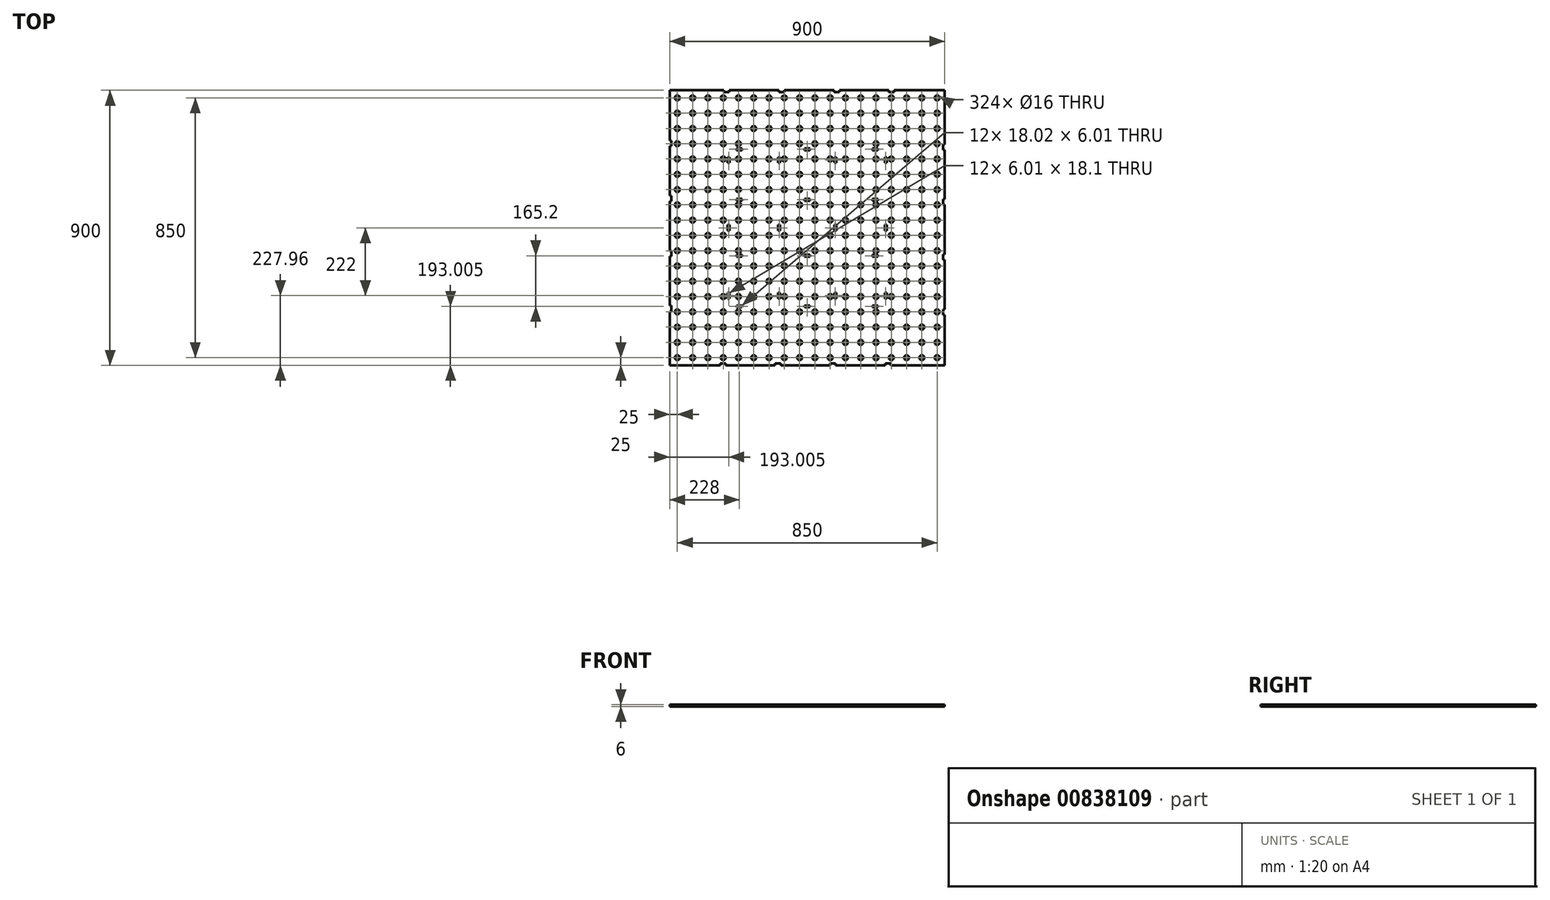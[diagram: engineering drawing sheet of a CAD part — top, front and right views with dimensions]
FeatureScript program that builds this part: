
annotation { "Feature Type Name" : "Feature", "Feature Type Description" : "" }
export const myFeature = defineFeature(function(context is Context, id is Id, definition is map)
    precondition{}
    {
        {
            var Q0;
            Q0=qCreatedBy(makeId("Top.planeOp"),FACE);
            var sketch = newSketch(context, id + "F0", { "sketchPlane" : qUnion([Q0])});
            skCircle(sketch, "E0", {"center": v(0, 0) * mm, "radius": 8 * mm});
            skCircle(sketch, "E1", {"center": v(50, 0) * mm, "radius": 8 * mm});
            skCircle(sketch, "E2", {"center": v(100, 0) * mm, "radius": 8 * mm});
            skCircle(sketch, "E3", {"center": v(0, -50) * mm, "radius": 8 * mm});
            skLineSegment(sketch, "E4", {"start": v(-25, 0.08) * mm, "end": v(875, 0.08) * mm, "construction": true});
            skCircle(sketch, "E5", {"center": v(150, 0.08) * mm, "radius": 8 * mm});
            skCircle(sketch, "E6", {"center": v(200, 0.08) * mm, "radius": 8 * mm});
            skCircle(sketch, "E7", {"center": v(250, 0.08) * mm, "radius": 8 * mm});
            skLineSegment(sketch, "E8", {"start": v(0, 8) * mm, "end": v(0, -874.92) * mm, "construction": true});
            skCircle(sketch, "E9", {"center": v(50, -50) * mm, "radius": 8 * mm});
            skCircle(sketch, "E10", {"center": v(100, -50) * mm, "radius": 8 * mm});
            skCircle(sketch, "E11", {"center": v(150, -50) * mm, "radius": 8 * mm});
            skCircle(sketch, "E12", {"center": v(200, -50) * mm, "radius": 8 * mm});
            skCircle(sketch, "E13", {"center": v(250, -50) * mm, "radius": 8 * mm});
            skCircle(sketch, "E14", {"center": v(0, -100) * mm, "radius": 8 * mm});
            skCircle(sketch, "E15", {"center": v(0, -150) * mm, "radius": 8 * mm});
            skCircle(sketch, "E16", {"center": v(0, -199.92) * mm, "radius": 8 * mm});
            skCircle(sketch, "E17", {"center": v(50, -100) * mm, "radius": 8 * mm});
            skCircle(sketch, "E18", {"center": v(100, -100) * mm, "radius": 8 * mm});
            skCircle(sketch, "E19", {"center": v(50, -150) * mm, "radius": 8 * mm});
            skCircle(sketch, "E20", {"center": v(100, -150) * mm, "radius": 8 * mm});
            skCircle(sketch, "E21", {"center": v(50, -199.92) * mm, "radius": 8 * mm});
            skCircle(sketch, "E22", {"center": v(100, -199.92) * mm, "radius": 8 * mm});
            skCircle(sketch, "E23", {"center": v(150, -100) * mm, "radius": 8 * mm});
            skCircle(sketch, "E24", {"center": v(150, -150) * mm, "radius": 8 * mm});
            skPoint(sketch, "E25.center.orphan", {"position": v(150, -199.92) * mm});
            skCircle(sketch, "E26", {"center": v(150, -199.92) * mm, "radius": 8 * mm});
            skCircle(sketch, "E27", {"center": v(200, -100) * mm, "radius": 8 * mm});
            skCircle(sketch, "E28", {"center": v(200, -150) * mm, "radius": 8 * mm});
            skCircle(sketch, "E29", {"center": v(250, -100) * mm, "radius": 8 * mm});
            skCircle(sketch, "E30", {"center": v(250, -150) * mm, "radius": 8 * mm});
            skCircle(sketch, "E31", {"center": v(200, -199.92) * mm, "radius": 8 * mm});
            skCircle(sketch, "E32", {"center": v(250, -199.92) * mm, "radius": 8 * mm});
            skCircle(sketch, "E33", {"center": v(300, 0.08) * mm, "radius": 8 * mm});
            skCircle(sketch, "E34", {"center": v(350, 0.08) * mm, "radius": 8 * mm});
            skCircle(sketch, "E35", {"center": v(400, 0.08) * mm, "radius": 8 * mm});
            skCircle(sketch, "E36", {"center": v(300, -50) * mm, "radius": 8 * mm});
            skCircle(sketch, "E37", {"center": v(350, -50) * mm, "radius": 8 * mm});
            skCircle(sketch, "E38", {"center": v(400, -50) * mm, "radius": 8 * mm});
            skCircle(sketch, "E39", {"center": v(300, -100) * mm, "radius": 8 * mm});
            skCircle(sketch, "E40", {"center": v(350, -100) * mm, "radius": 8 * mm});
            skCircle(sketch, "E41", {"center": v(400, -100) * mm, "radius": 8 * mm});
            skCircle(sketch, "E42", {"center": v(300, -150) * mm, "radius": 8 * mm});
            skCircle(sketch, "E43", {"center": v(350, -150) * mm, "radius": 8 * mm});
            skCircle(sketch, "E44", {"center": v(400, -150) * mm, "radius": 8 * mm});
            skCircle(sketch, "E45", {"center": v(300, -199.92) * mm, "radius": 8 * mm});
            skCircle(sketch, "E46", {"center": v(350, -199.92) * mm, "radius": 8 * mm});
            skCircle(sketch, "E47", {"center": v(400, -199.92) * mm, "radius": 8 * mm});
            skCircle(sketch, "E48", {"center": v(0, -249.92) * mm, "radius": 8 * mm});
            skCircle(sketch, "E49", {"center": v(0, -299.92) * mm, "radius": 8 * mm});
            skCircle(sketch, "E50", {"center": v(0, -349.92) * mm, "radius": 8 * mm});
            skCircle(sketch, "E51", {"center": v(50, -249.92) * mm, "radius": 8 * mm});
            skCircle(sketch, "E52", {"center": v(100, -249.92) * mm, "radius": 8 * mm});
            skCircle(sketch, "E53", {"center": v(50, -299.92) * mm, "radius": 8 * mm});
            skCircle(sketch, "E54", {"center": v(100, -299.92) * mm, "radius": 8 * mm});
            skCircle(sketch, "E55", {"center": v(50, -349.92) * mm, "radius": 8 * mm});
            skCircle(sketch, "E56", {"center": v(100, -349.92) * mm, "radius": 8 * mm});
            skCircle(sketch, "E57", {"center": v(200, -249.92) * mm, "radius": 8 * mm});
            skCircle(sketch, "E58", {"center": v(150, -249.92) * mm, "radius": 8 * mm});
            skCircle(sketch, "E59", {"center": v(150, -299.92) * mm, "radius": 8 * mm});
            skCircle(sketch, "E60", {"center": v(200, -299.92) * mm, "radius": 8 * mm});
            skCircle(sketch, "E61", {"center": v(150, -349.92) * mm, "radius": 8 * mm});
            skCircle(sketch, "E62", {"center": v(200, -349.92) * mm, "radius": 8 * mm});
            skCircle(sketch, "E63", {"center": v(250, -249.92) * mm, "radius": 8 * mm});
            skCircle(sketch, "E64", {"center": v(300, -249.92) * mm, "radius": 8 * mm});
            skCircle(sketch, "E65", {"center": v(350, -249.92) * mm, "radius": 8 * mm});
            skCircle(sketch, "E66", {"center": v(400, -249.92) * mm, "radius": 8 * mm});
            skCircle(sketch, "E67", {"center": v(250, -299.92) * mm, "radius": 8 * mm});
            skCircle(sketch, "E68", {"center": v(300, -299.92) * mm, "radius": 8 * mm});
            skCircle(sketch, "E69", {"center": v(350, -299.92) * mm, "radius": 8 * mm});
            skCircle(sketch, "E70", {"center": v(400, -299.92) * mm, "radius": 8 * mm});
            skCircle(sketch, "E71", {"center": v(250, -349.92) * mm, "radius": 8 * mm});
            skCircle(sketch, "E72", {"center": v(300, -349.92) * mm, "radius": 8 * mm});
            skCircle(sketch, "E73", {"center": v(350, -349.92) * mm, "radius": 8 * mm});
            skCircle(sketch, "E74", {"center": v(400, -349.92) * mm, "radius": 8 * mm});
            skCircle(sketch, "E75", {"center": v(450, 0.08) * mm, "radius": 8 * mm});
            skCircle(sketch, "E76", {"center": v(500, 0.08) * mm, "radius": 8 * mm});
            skCircle(sketch, "E77", {"center": v(550, 0.08) * mm, "radius": 8 * mm});
            skCircle(sketch, "E78", {"center": v(600, 0.08) * mm, "radius": 8 * mm});
            skCircle(sketch, "E79", {"center": v(650, 0.08) * mm, "radius": 8 * mm});
            skCircle(sketch, "E80", {"center": v(700, 0.08) * mm, "radius": 8 * mm});
            skCircle(sketch, "E81", {"center": v(750, 0.08) * mm, "radius": 8 * mm});
            skCircle(sketch, "E82", {"center": v(800, 0.08) * mm, "radius": 8 * mm});
            skCircle(sketch, "E83", {"center": v(850, 0.08) * mm, "radius": 8 * mm});
            skCircle(sketch, "E84", {"center": v(0, -399.92) * mm, "radius": 8 * mm});
            skCircle(sketch, "E85", {"center": v(0, -449.92) * mm, "radius": 8 * mm});
            skCircle(sketch, "E86", {"center": v(0, -499.92) * mm, "radius": 8 * mm});
            skCircle(sketch, "E87", {"center": v(0, -549.92) * mm, "radius": 8 * mm});
            skCircle(sketch, "E88", {"center": v(0, -599.92) * mm, "radius": 8 * mm});
            skCircle(sketch, "E89", {"center": v(0, -649.92) * mm, "radius": 8 * mm});
            skCircle(sketch, "E90", {"center": v(0, -699.92) * mm, "radius": 8 * mm});
            skCircle(sketch, "E91", {"center": v(0, -749.92) * mm, "radius": 8 * mm});
            skCircle(sketch, "E92", {"center": v(0, -799.92) * mm, "radius": 8 * mm});
            skCircle(sketch, "E93", {"center": v(0, -849.92) * mm, "radius": 8 * mm});
            skCircle(sketch, "E94", {"center": v(450, -50) * mm, "radius": 8 * mm});
            skCircle(sketch, "E95", {"center": v(450, -100) * mm, "radius": 8 * mm});
            skCircle(sketch, "E96", {"center": v(500, -50) * mm, "radius": 8 * mm});
            skCircle(sketch, "E97", {"center": v(500, -100) * mm, "radius": 8 * mm});
            skCircle(sketch, "E98", {"center": v(550, -50) * mm, "radius": 8 * mm});
            skCircle(sketch, "E99", {"center": v(550, -100) * mm, "radius": 8 * mm});
            skCircle(sketch, "E100", {"center": v(600, -50) * mm, "radius": 8 * mm});
            skCircle(sketch, "E101", {"center": v(650, -50) * mm, "radius": 8 * mm});
            skCircle(sketch, "E102", {"center": v(700, -50) * mm, "radius": 8 * mm});
            skCircle(sketch, "E103", {"center": v(600, -100) * mm, "radius": 8 * mm});
            skCircle(sketch, "E104", {"center": v(650, -100) * mm, "radius": 8 * mm});
            skCircle(sketch, "E105", {"center": v(700, -100) * mm, "radius": 8 * mm});
            skCircle(sketch, "E106", {"center": v(450, -150) * mm, "radius": 8 * mm});
            skCircle(sketch, "E107", {"center": v(500, -150) * mm, "radius": 8 * mm});
            skCircle(sketch, "E108", {"center": v(550, -150) * mm, "radius": 8 * mm});
            skCircle(sketch, "E109", {"center": v(600, -150) * mm, "radius": 8 * mm});
            skCircle(sketch, "E110", {"center": v(650, -150) * mm, "radius": 8 * mm});
            skCircle(sketch, "E111", {"center": v(700, -150) * mm, "radius": 8 * mm});
            skCircle(sketch, "E112", {"center": v(450, -199.92) * mm, "radius": 8 * mm});
            skCircle(sketch, "E113", {"center": v(500, -199.92) * mm, "radius": 8 * mm});
            skCircle(sketch, "E114", {"center": v(550, -199.92) * mm, "radius": 8 * mm});
            skCircle(sketch, "E115", {"center": v(600, -199.92) * mm, "radius": 8 * mm});
            skCircle(sketch, "E116", {"center": v(650, -199.92) * mm, "radius": 8 * mm});
            skCircle(sketch, "E117", {"center": v(450, -249.92) * mm, "radius": 8 * mm});
            skCircle(sketch, "E118", {"center": v(500, -249.92) * mm, "radius": 8 * mm});
            skCircle(sketch, "E119", {"center": v(550, -249.92) * mm, "radius": 8 * mm});
            skCircle(sketch, "E120", {"center": v(600, -249.92) * mm, "radius": 8 * mm});
            skCircle(sketch, "E121", {"center": v(650, -249.92) * mm, "radius": 8 * mm});
            skCircle(sketch, "E122", {"center": v(450, -299.92) * mm, "radius": 8 * mm});
            skCircle(sketch, "E123", {"center": v(500, -299.92) * mm, "radius": 8 * mm});
            skCircle(sketch, "E124", {"center": v(550, -299.92) * mm, "radius": 8 * mm});
            skCircle(sketch, "E125", {"center": v(600, -299.92) * mm, "radius": 8 * mm});
            skCircle(sketch, "E126", {"center": v(650, -299.92) * mm, "radius": 8 * mm});
            skCircle(sketch, "E127", {"center": v(750, -50) * mm, "radius": 8 * mm});
            skCircle(sketch, "E128", {"center": v(800, -50) * mm, "radius": 8 * mm});
            skCircle(sketch, "E129", {"center": v(850, -50) * mm, "radius": 8 * mm});
            skCircle(sketch, "E130", {"center": v(750, -100) * mm, "radius": 8 * mm});
            skCircle(sketch, "E131", {"center": v(800, -100) * mm, "radius": 8 * mm});
            skCircle(sketch, "E132", {"center": v(850, -100) * mm, "radius": 8 * mm});
            skCircle(sketch, "E133", {"center": v(750, -150) * mm, "radius": 8 * mm});
            skCircle(sketch, "E134", {"center": v(800, -150) * mm, "radius": 8 * mm});
            skCircle(sketch, "E135", {"center": v(850, -150) * mm, "radius": 8 * mm});
            skCircle(sketch, "E136", {"center": v(700, -199.92) * mm, "radius": 8 * mm});
            skCircle(sketch, "E137", {"center": v(750, -199.92) * mm, "radius": 8 * mm});
            skCircle(sketch, "E138", {"center": v(800, -199.92) * mm, "radius": 8 * mm});
            skCircle(sketch, "E139", {"center": v(850, -199.92) * mm, "radius": 8 * mm});
            skCircle(sketch, "E140", {"center": v(700, -249.92) * mm, "radius": 8 * mm});
            skCircle(sketch, "E141", {"center": v(750, -249.92) * mm, "radius": 8 * mm});
            skCircle(sketch, "E142", {"center": v(800, -249.92) * mm, "radius": 8 * mm});
            skCircle(sketch, "E143", {"center": v(850, -249.92) * mm, "radius": 8 * mm});
            skCircle(sketch, "E144", {"center": v(700, -299.92) * mm, "radius": 8 * mm});
            skCircle(sketch, "E145", {"center": v(750, -299.92) * mm, "radius": 8 * mm});
            skCircle(sketch, "E146", {"center": v(800, -299.92) * mm, "radius": 8 * mm});
            skCircle(sketch, "E147", {"center": v(850, -299.92) * mm, "radius": 8 * mm});
            skCircle(sketch, "E148", {"center": v(450, -349.92) * mm, "radius": 8 * mm});
            skCircle(sketch, "E149", {"center": v(500, -349.92) * mm, "radius": 8 * mm});
            skCircle(sketch, "E150", {"center": v(550, -349.92) * mm, "radius": 8 * mm});
            skCircle(sketch, "E151", {"center": v(600, -349.92) * mm, "radius": 8 * mm});
            skCircle(sketch, "E152", {"center": v(650, -349.92) * mm, "radius": 8 * mm});
            skCircle(sketch, "E153", {"center": v(700, -349.92) * mm, "radius": 8 * mm});
            skCircle(sketch, "E154", {"center": v(750, -349.92) * mm, "radius": 8 * mm});
            skCircle(sketch, "E155", {"center": v(800, -349.92) * mm, "radius": 8 * mm});
            skCircle(sketch, "E156", {"center": v(850, -349.92) * mm, "radius": 8 * mm});
            skCircle(sketch, "E157", {"center": v(50, -399.92) * mm, "radius": 8 * mm});
            skCircle(sketch, "E158", {"center": v(100, -399.92) * mm, "radius": 8 * mm});
            skCircle(sketch, "E159", {"center": v(150, -399.92) * mm, "radius": 8 * mm});
            skCircle(sketch, "E160", {"center": v(200, -399.92) * mm, "radius": 8 * mm});
            skCircle(sketch, "E161", {"center": v(250, -399.92) * mm, "radius": 8 * mm});
            skCircle(sketch, "E162", {"center": v(300, -399.92) * mm, "radius": 8 * mm});
            skCircle(sketch, "E163", {"center": v(350, -399.92) * mm, "radius": 8 * mm});
            skCircle(sketch, "E164", {"center": v(400, -399.92) * mm, "radius": 8 * mm});
            skCircle(sketch, "E165", {"center": v(450, -399.92) * mm, "radius": 8 * mm});
            skCircle(sketch, "E166", {"center": v(500, -399.92) * mm, "radius": 8 * mm});
            skCircle(sketch, "E167", {"center": v(550, -399.92) * mm, "radius": 8 * mm});
            skCircle(sketch, "E168", {"center": v(600, -399.92) * mm, "radius": 8 * mm});
            skCircle(sketch, "E169", {"center": v(650, -399.92) * mm, "radius": 8 * mm});
            skCircle(sketch, "E170", {"center": v(700, -399.92) * mm, "radius": 8 * mm});
            skCircle(sketch, "E171", {"center": v(750, -399.92) * mm, "radius": 8 * mm});
            skCircle(sketch, "E172", {"center": v(800, -399.92) * mm, "radius": 8 * mm});
            skCircle(sketch, "E173", {"center": v(850, -399.92) * mm, "radius": 8 * mm});
            skCircle(sketch, "E174", {"center": v(50, -449.92) * mm, "radius": 8 * mm});
            skCircle(sketch, "E175", {"center": v(100, -449.92) * mm, "radius": 8 * mm});
            skCircle(sketch, "E176", {"center": v(150, -449.92) * mm, "radius": 8 * mm});
            skCircle(sketch, "E177", {"center": v(200, -449.92) * mm, "radius": 8 * mm});
            skCircle(sketch, "E178", {"center": v(250, -449.92) * mm, "radius": 8 * mm});
            skCircle(sketch, "E179", {"center": v(300, -449.92) * mm, "radius": 8 * mm});
            skCircle(sketch, "E180", {"center": v(350, -449.92) * mm, "radius": 8 * mm});
            skCircle(sketch, "E181", {"center": v(400, -449.92) * mm, "radius": 8 * mm});
            skCircle(sketch, "E182", {"center": v(450, -449.92) * mm, "radius": 8 * mm});
            skCircle(sketch, "E183", {"center": v(500, -449.92) * mm, "radius": 8 * mm});
            skCircle(sketch, "E184", {"center": v(550, -449.92) * mm, "radius": 8 * mm});
            skCircle(sketch, "E185", {"center": v(600, -449.92) * mm, "radius": 8 * mm});
            skCircle(sketch, "E186", {"center": v(650, -449.92) * mm, "radius": 8 * mm});
            skCircle(sketch, "E187", {"center": v(700, -449.92) * mm, "radius": 8 * mm});
            skCircle(sketch, "E188", {"center": v(750, -449.92) * mm, "radius": 8 * mm});
            skCircle(sketch, "E189", {"center": v(800, -449.92) * mm, "radius": 8 * mm});
            skCircle(sketch, "E190", {"center": v(850, -449.92) * mm, "radius": 8 * mm});
            skCircle(sketch, "E191", {"center": v(50, -499.92) * mm, "radius": 8 * mm});
            skCircle(sketch, "E192", {"center": v(100, -499.92) * mm, "radius": 8 * mm});
            skCircle(sketch, "E193", {"center": v(150, -499.92) * mm, "radius": 8 * mm});
            skCircle(sketch, "E194", {"center": v(200, -499.92) * mm, "radius": 8 * mm});
            skCircle(sketch, "E195", {"center": v(250, -499.92) * mm, "radius": 8 * mm});
            skCircle(sketch, "E196", {"center": v(300, -499.92) * mm, "radius": 8 * mm});
            skCircle(sketch, "E197", {"center": v(350, -499.92) * mm, "radius": 8 * mm});
            skCircle(sketch, "E198", {"center": v(400, -499.92) * mm, "radius": 8 * mm});
            skCircle(sketch, "E199", {"center": v(450, -499.92) * mm, "radius": 8 * mm});
            skCircle(sketch, "E200", {"center": v(500, -499.92) * mm, "radius": 8 * mm});
            skCircle(sketch, "E201", {"center": v(550, -499.92) * mm, "radius": 8 * mm});
            skCircle(sketch, "E202", {"center": v(600, -499.92) * mm, "radius": 8 * mm});
            skCircle(sketch, "E203", {"center": v(650, -499.92) * mm, "radius": 8 * mm});
            skCircle(sketch, "E204", {"center": v(700, -499.92) * mm, "radius": 8 * mm});
            skCircle(sketch, "E205", {"center": v(750, -499.92) * mm, "radius": 8 * mm});
            skCircle(sketch, "E206", {"center": v(800, -499.92) * mm, "radius": 8 * mm});
            skCircle(sketch, "E207", {"center": v(850, -499.92) * mm, "radius": 8 * mm});
            skCircle(sketch, "E208", {"center": v(50, -549.92) * mm, "radius": 8 * mm});
            skCircle(sketch, "E209", {"center": v(100, -549.92) * mm, "radius": 8 * mm});
            skCircle(sketch, "E210", {"center": v(150, -549.92) * mm, "radius": 8 * mm});
            skCircle(sketch, "E211", {"center": v(200, -549.92) * mm, "radius": 8 * mm});
            skCircle(sketch, "E212", {"center": v(250, -549.92) * mm, "radius": 8 * mm});
            skCircle(sketch, "E213", {"center": v(300, -549.92) * mm, "radius": 8 * mm});
            skCircle(sketch, "E214", {"center": v(350, -549.92) * mm, "radius": 8 * mm});
            skCircle(sketch, "E215", {"center": v(400, -549.92) * mm, "radius": 8 * mm});
            skCircle(sketch, "E216", {"center": v(450, -549.92) * mm, "radius": 8 * mm});
            skCircle(sketch, "E217", {"center": v(500, -549.92) * mm, "radius": 8 * mm});
            skCircle(sketch, "E218", {"center": v(550, -549.92) * mm, "radius": 8 * mm});
            skCircle(sketch, "E219", {"center": v(600, -549.92) * mm, "radius": 8 * mm});
            skCircle(sketch, "E220", {"center": v(650, -549.92) * mm, "radius": 8 * mm});
            skCircle(sketch, "E221", {"center": v(700, -549.92) * mm, "radius": 8 * mm});
            skCircle(sketch, "E222", {"center": v(750, -549.92) * mm, "radius": 8 * mm});
            skCircle(sketch, "E223", {"center": v(800, -549.92) * mm, "radius": 8 * mm});
            skCircle(sketch, "E224", {"center": v(850, -549.92) * mm, "radius": 8 * mm});
            skCircle(sketch, "E225", {"center": v(50, -599.92) * mm, "radius": 8 * mm});
            skCircle(sketch, "E226", {"center": v(50, -649.92) * mm, "radius": 8 * mm});
            skCircle(sketch, "E227", {"center": v(50, -699.92) * mm, "radius": 8 * mm});
            skCircle(sketch, "E228", {"center": v(50, -749.92) * mm, "radius": 8 * mm});
            skCircle(sketch, "E229", {"center": v(50, -799.92) * mm, "radius": 8 * mm});
            skCircle(sketch, "E230", {"center": v(50, -849.92) * mm, "radius": 8 * mm});
            skCircle(sketch, "E231", {"center": v(100, -599.92) * mm, "radius": 8 * mm});
            skCircle(sketch, "E232", {"center": v(100, -649.92) * mm, "radius": 8 * mm});
            skCircle(sketch, "E233", {"center": v(100, -699.92) * mm, "radius": 8 * mm});
            skCircle(sketch, "E234", {"center": v(100, -749.92) * mm, "radius": 8 * mm});
            skCircle(sketch, "E235", {"center": v(100, -799.92) * mm, "radius": 8 * mm});
            skCircle(sketch, "E236", {"center": v(100, -849.92) * mm, "radius": 8 * mm});
            skCircle(sketch, "E237", {"center": v(150, -599.92) * mm, "radius": 8 * mm});
            skCircle(sketch, "E238", {"center": v(150, -649.92) * mm, "radius": 8 * mm});
            skCircle(sketch, "E239", {"center": v(150, -699.92) * mm, "radius": 8 * mm});
            skCircle(sketch, "E240", {"center": v(150, -749.92) * mm, "radius": 8 * mm});
            skCircle(sketch, "E241", {"center": v(150, -799.92) * mm, "radius": 8 * mm});
            skCircle(sketch, "E242", {"center": v(150, -849.92) * mm, "radius": 8 * mm});
            skCircle(sketch, "E243", {"center": v(200, -599.92) * mm, "radius": 8 * mm});
            skCircle(sketch, "E244", {"center": v(250, -599.92) * mm, "radius": 8 * mm});
            skCircle(sketch, "E245", {"center": v(300, -599.92) * mm, "radius": 8 * mm});
            skCircle(sketch, "E246", {"center": v(350, -599.92) * mm, "radius": 8 * mm});
            skCircle(sketch, "E247", {"center": v(400, -599.92) * mm, "radius": 8 * mm});
            skCircle(sketch, "E248", {"center": v(450, -599.92) * mm, "radius": 8 * mm});
            skCircle(sketch, "E249", {"center": v(500, -599.92) * mm, "radius": 8 * mm});
            skCircle(sketch, "E250", {"center": v(550, -599.92) * mm, "radius": 8 * mm});
            skCircle(sketch, "E251", {"center": v(600, -599.92) * mm, "radius": 8 * mm});
            skCircle(sketch, "E252", {"center": v(650, -599.92) * mm, "radius": 8 * mm});
            skCircle(sketch, "E253", {"center": v(700, -599.92) * mm, "radius": 8 * mm});
            skCircle(sketch, "E254", {"center": v(750, -599.92) * mm, "radius": 8 * mm});
            skCircle(sketch, "E255", {"center": v(800, -599.92) * mm, "radius": 8 * mm});
            skCircle(sketch, "E256", {"center": v(850, -599.92) * mm, "radius": 8 * mm});
            skCircle(sketch, "E257", {"center": v(200, -649.92) * mm, "radius": 8 * mm});
            skCircle(sketch, "E258", {"center": v(250, -649.92) * mm, "radius": 8 * mm});
            skCircle(sketch, "E259", {"center": v(300, -649.92) * mm, "radius": 8 * mm});
            skCircle(sketch, "E260", {"center": v(350, -649.92) * mm, "radius": 8 * mm});
            skCircle(sketch, "E261", {"center": v(400, -649.92) * mm, "radius": 8 * mm});
            skCircle(sketch, "E262", {"center": v(450, -649.92) * mm, "radius": 8 * mm});
            skCircle(sketch, "E263", {"center": v(500, -649.92) * mm, "radius": 8 * mm});
            skCircle(sketch, "E264", {"center": v(550, -649.92) * mm, "radius": 8 * mm});
            skCircle(sketch, "E265", {"center": v(600, -649.92) * mm, "radius": 8 * mm});
            skCircle(sketch, "E266", {"center": v(650, -649.92) * mm, "radius": 8 * mm});
            skCircle(sketch, "E267", {"center": v(700, -649.92) * mm, "radius": 8 * mm});
            skCircle(sketch, "E268", {"center": v(750, -649.92) * mm, "radius": 8 * mm});
            skCircle(sketch, "E269", {"center": v(800, -649.92) * mm, "radius": 8 * mm});
            skCircle(sketch, "E270", {"center": v(850, -649.92) * mm, "radius": 8 * mm});
            skCircle(sketch, "E271", {"center": v(850, -699.92) * mm, "radius": 8 * mm});
            skCircle(sketch, "E272", {"center": v(800, -699.92) * mm, "radius": 8 * mm});
            skCircle(sketch, "E273", {"center": v(750, -699.92) * mm, "radius": 8 * mm});
            skCircle(sketch, "E274", {"center": v(700, -699.92) * mm, "radius": 8 * mm});
            skCircle(sketch, "E275", {"center": v(650, -699.92) * mm, "radius": 8 * mm});
            skCircle(sketch, "E276", {"center": v(600, -699.92) * mm, "radius": 8 * mm});
            skCircle(sketch, "E277", {"center": v(550, -699.92) * mm, "radius": 8 * mm});
            skCircle(sketch, "E278", {"center": v(500, -699.92) * mm, "radius": 8 * mm});
            skCircle(sketch, "E279", {"center": v(450, -699.92) * mm, "radius": 8 * mm});
            skCircle(sketch, "E280", {"center": v(400, -699.92) * mm, "radius": 8 * mm});
            skCircle(sketch, "E281", {"center": v(350, -699.92) * mm, "radius": 8 * mm});
            skCircle(sketch, "E282", {"center": v(300, -699.92) * mm, "radius": 8 * mm});
            skCircle(sketch, "E283", {"center": v(250, -699.92) * mm, "radius": 8 * mm});
            skCircle(sketch, "E284", {"center": v(200, -699.92) * mm, "radius": 8 * mm});
            skCircle(sketch, "E285", {"center": v(850, -749.92) * mm, "radius": 8 * mm});
            skCircle(sketch, "E286", {"center": v(800, -749.92) * mm, "radius": 8 * mm});
            skCircle(sketch, "E287", {"center": v(750, -749.92) * mm, "radius": 8 * mm});
            skCircle(sketch, "E288", {"center": v(700, -749.92) * mm, "radius": 8 * mm});
            skCircle(sketch, "E289", {"center": v(650, -749.92) * mm, "radius": 8 * mm});
            skCircle(sketch, "E290", {"center": v(600, -749.92) * mm, "radius": 8 * mm});
            skCircle(sketch, "E291", {"center": v(550, -749.92) * mm, "radius": 8 * mm});
            skCircle(sketch, "E292", {"center": v(500, -749.92) * mm, "radius": 8 * mm});
            skCircle(sketch, "E293", {"center": v(450, -749.92) * mm, "radius": 8 * mm});
            skCircle(sketch, "E294", {"center": v(400, -749.92) * mm, "radius": 8 * mm});
            skCircle(sketch, "E295", {"center": v(350, -749.92) * mm, "radius": 8 * mm});
            skCircle(sketch, "E296", {"center": v(300, -749.92) * mm, "radius": 8 * mm});
            skCircle(sketch, "E297", {"center": v(250, -749.92) * mm, "radius": 8 * mm});
            skCircle(sketch, "E298", {"center": v(200, -749.92) * mm, "radius": 8 * mm});
            skCircle(sketch, "E299", {"center": v(850, -799.92) * mm, "radius": 8 * mm});
            skCircle(sketch, "E300", {"center": v(800, -799.92) * mm, "radius": 8 * mm});
            skCircle(sketch, "E301", {"center": v(750, -799.92) * mm, "radius": 8 * mm});
            skCircle(sketch, "E302", {"center": v(700, -799.92) * mm, "radius": 8 * mm});
            skCircle(sketch, "E303", {"center": v(650, -799.92) * mm, "radius": 8 * mm});
            skCircle(sketch, "E304", {"center": v(600, -799.92) * mm, "radius": 8 * mm});
            skCircle(sketch, "E305", {"center": v(550, -799.92) * mm, "radius": 8 * mm});
            skCircle(sketch, "E306", {"center": v(500, -799.92) * mm, "radius": 8 * mm});
            skCircle(sketch, "E307", {"center": v(450, -799.92) * mm, "radius": 8 * mm});
            skCircle(sketch, "E308", {"center": v(400, -799.92) * mm, "radius": 8 * mm});
            skCircle(sketch, "E309", {"center": v(350, -799.92) * mm, "radius": 8 * mm});
            skCircle(sketch, "E310", {"center": v(300, -799.92) * mm, "radius": 8 * mm});
            skCircle(sketch, "E311", {"center": v(250, -799.92) * mm, "radius": 8 * mm});
            skCircle(sketch, "E312", {"center": v(200, -799.92) * mm, "radius": 8 * mm});
            skCircle(sketch, "E313", {"center": v(850, -849.92) * mm, "radius": 8 * mm});
            skCircle(sketch, "E314", {"center": v(800, -849.92) * mm, "radius": 8 * mm});
            skCircle(sketch, "E315", {"center": v(750, -849.92) * mm, "radius": 8 * mm});
            skCircle(sketch, "E316", {"center": v(700, -849.92) * mm, "radius": 8 * mm});
            skCircle(sketch, "E317", {"center": v(650, -849.92) * mm, "radius": 8 * mm});
            skCircle(sketch, "E318", {"center": v(600, -849.92) * mm, "radius": 8 * mm});
            skCircle(sketch, "E319", {"center": v(550, -849.92) * mm, "radius": 8 * mm});
            skCircle(sketch, "E320", {"center": v(500, -849.92) * mm, "radius": 8 * mm});
            skCircle(sketch, "E321", {"center": v(450, -849.92) * mm, "radius": 8 * mm});
            skCircle(sketch, "E322", {"center": v(400, -849.92) * mm, "radius": 8 * mm});
            skCircle(sketch, "E323", {"center": v(350, -849.92) * mm, "radius": 8 * mm});
            skCircle(sketch, "E324", {"center": v(300, -849.92) * mm, "radius": 8 * mm});
            skCircle(sketch, "E325", {"center": v(250, -849.92) * mm, "radius": 8 * mm});
            skCircle(sketch, "E326", {"center": v(200, -849.92) * mm, "radius": 8 * mm});
            skLineSegment(sketch, "E327.top", {"start": v(-25, -874.92) * mm, "end": v(140, -874.92) * mm});
            skLineSegment(sketch, "E327.left", {"start": v(-25, 25.08) * mm, "end": v(-25, -139.92) * mm});
            skLineSegment(sketch, "E327.right", {"start": v(875, 25.08) * mm, "end": v(875, -151.82) * mm});
            skLineSegment(sketch, "E328.top", {"start": v(140, -868.91) * mm, "end": v(158.1, -868.91) * mm});
            skLineSegment(sketch, "E328.left", {"start": v(140, -874.92) * mm, "end": v(140, -868.91) * mm});
            skLineSegment(sketch, "E328.right", {"start": v(158.1, -874.92) * mm, "end": v(158.1, -868.91) * mm});
            skLineSegment(sketch, "E329.top", {"start": v(320, -868.91) * mm, "end": v(338.1, -868.91) * mm});
            skLineSegment(sketch, "E329.left", {"start": v(320, -874.92) * mm, "end": v(320, -868.91) * mm});
            skLineSegment(sketch, "E329.right", {"start": v(338.1, -874.92) * mm, "end": v(338.1, -868.91) * mm});
            skLineSegment(sketch, "E330.top", {"start": v(500, -868.91) * mm, "end": v(518.1, -868.91) * mm});
            skLineSegment(sketch, "E330.left", {"start": v(500, -874.92) * mm, "end": v(500, -868.91) * mm});
            skLineSegment(sketch, "E330.right", {"start": v(518.1, -874.92) * mm, "end": v(518.1, -868.91) * mm});
            skLineSegment(sketch, "E331.trimOffspring", {"start": v(158.1, -874.92) * mm, "end": v(320, -874.92) * mm});
            skLineSegment(sketch, "E332.trimOffspring", {"start": v(338.1, -874.92) * mm, "end": v(500, -874.92) * mm});
            skLineSegment(sketch, "E333.trimOffspring", {"start": v(518.1, -874.92) * mm, "end": v(680, -874.92) * mm});
            skLineSegment(sketch, "E334", {"start": v(-25, 25.08) * mm, "end": v(151.9, 25.08) * mm});
            skLineSegment(sketch, "E335.top", {"start": v(680, -868.91) * mm, "end": v(698.1, -868.91) * mm});
            skLineSegment(sketch, "E335.left", {"start": v(680, -874.92) * mm, "end": v(680, -868.91) * mm});
            skLineSegment(sketch, "E335.right", {"start": v(698.1, -874.92) * mm, "end": v(698.1, -868.91) * mm});
            skLineSegment(sketch, "E336.trimOffspring", {"start": v(698.1, -874.92) * mm, "end": v(875, -874.92) * mm});
            skLineSegment(sketch, "E337.bottom", {"start": v(875, -151.82) * mm, "end": v(869, -151.82) * mm});
            skLineSegment(sketch, "E337.top", {"start": v(875, -169.92) * mm, "end": v(869, -169.92) * mm});
            skLineSegment(sketch, "E337.right", {"start": v(869, -151.82) * mm, "end": v(869, -169.92) * mm});
            skLineSegment(sketch, "E338.bottom", {"start": v(875, -331.82) * mm, "end": v(869, -331.82) * mm});
            skLineSegment(sketch, "E338.top", {"start": v(875, -349.92) * mm, "end": v(869, -349.92) * mm});
            skLineSegment(sketch, "E338.right", {"start": v(869, -331.82) * mm, "end": v(869, -349.92) * mm});
            skLineSegment(sketch, "E339.bottom", {"start": v(875, -511.82) * mm, "end": v(869, -511.82) * mm});
            skLineSegment(sketch, "E339.top", {"start": v(875, -529.92) * mm, "end": v(869, -529.92) * mm});
            skLineSegment(sketch, "E339.right", {"start": v(869, -511.82) * mm, "end": v(869, -529.92) * mm});
            skLineSegment(sketch, "E340.bottom", {"start": v(875, -691.82) * mm, "end": v(869, -691.82) * mm});
            skLineSegment(sketch, "E340.top", {"start": v(875, -709.92) * mm, "end": v(869, -709.92) * mm});
            skLineSegment(sketch, "E340.right", {"start": v(869, -691.82) * mm, "end": v(869, -709.92) * mm});
            skLineSegment(sketch, "E341.trimOffspring", {"start": v(875, -169.92) * mm, "end": v(875, -331.82) * mm});
            skLineSegment(sketch, "E342.trimOffspring", {"start": v(875, -349.92) * mm, "end": v(875, -511.82) * mm});
            skLineSegment(sketch, "E343.trimOffspring", {"start": v(875, -529.92) * mm, "end": v(875, -691.82) * mm});
            skLineSegment(sketch, "E344.trimOffspring", {"start": v(875, -709.92) * mm, "end": v(875, -874.92) * mm});
            skLineSegment(sketch, "E345.bottom", {"start": v(-25, -698.02) * mm, "end": v(-18.99, -698.02) * mm});
            skLineSegment(sketch, "E345.top", {"start": v(-25, -679.92) * mm, "end": v(-18.99, -679.92) * mm});
            skLineSegment(sketch, "E345.right", {"start": v(-18.99, -698.02) * mm, "end": v(-18.99, -679.92) * mm});
            skLineSegment(sketch, "E346.bottom", {"start": v(-25, -518.02) * mm, "end": v(-18.99, -518.02) * mm});
            skLineSegment(sketch, "E346.top", {"start": v(-25, -499.92) * mm, "end": v(-18.99, -499.92) * mm});
            skLineSegment(sketch, "E346.right", {"start": v(-18.99, -518.02) * mm, "end": v(-18.99, -499.92) * mm});
            skLineSegment(sketch, "E347.bottom", {"start": v(-25, -338.02) * mm, "end": v(-18.99, -338.02) * mm});
            skLineSegment(sketch, "E347.top", {"start": v(-25, -319.92) * mm, "end": v(-18.99, -319.92) * mm});
            skLineSegment(sketch, "E347.right", {"start": v(-18.99, -338.02) * mm, "end": v(-18.99, -319.92) * mm});
            skLineSegment(sketch, "E348.bottom", {"start": v(-25, -158.02) * mm, "end": v(-18.99, -158.02) * mm});
            skLineSegment(sketch, "E348.top", {"start": v(-25, -139.92) * mm, "end": v(-18.99, -139.92) * mm});
            skLineSegment(sketch, "E348.right", {"start": v(-18.99, -158.02) * mm, "end": v(-18.99, -139.92) * mm});
            skLineSegment(sketch, "E349.trimOffspring", {"start": v(-25, -698.02) * mm, "end": v(-25, -874.92) * mm});
            skLineSegment(sketch, "E350.trimOffspring", {"start": v(-25, -518.02) * mm, "end": v(-25, -679.92) * mm});
            skLineSegment(sketch, "E351.trimOffspring", {"start": v(-25, -158.02) * mm, "end": v(-25, -319.92) * mm});
            skLineSegment(sketch, "E352.top", {"start": v(151.9, 19.07) * mm, "end": v(170, 19.07) * mm});
            skLineSegment(sketch, "E352.left", {"start": v(151.9, 25.08) * mm, "end": v(151.9, 19.07) * mm});
            skLineSegment(sketch, "E352.right", {"start": v(170, 25.08) * mm, "end": v(170, 19.07) * mm});
            skLineSegment(sketch, "E353.top", {"start": v(331.9, 19.07) * mm, "end": v(350, 19.07) * mm});
            skLineSegment(sketch, "E353.left", {"start": v(331.9, 25.08) * mm, "end": v(331.9, 19.07) * mm});
            skLineSegment(sketch, "E353.right", {"start": v(350, 25.08) * mm, "end": v(350, 19.07) * mm});
            skLineSegment(sketch, "E354.top", {"start": v(511.9, 19.07) * mm, "end": v(530, 19.07) * mm});
            skLineSegment(sketch, "E354.left", {"start": v(511.9, 25.08) * mm, "end": v(511.9, 19.07) * mm});
            skLineSegment(sketch, "E354.right", {"start": v(530, 25.08) * mm, "end": v(530, 19.07) * mm});
            skLineSegment(sketch, "E355.top", {"start": v(691.9, 19.07) * mm, "end": v(710, 19.07) * mm});
            skLineSegment(sketch, "E355.left", {"start": v(691.9, 25.08) * mm, "end": v(691.9, 19.07) * mm});
            skLineSegment(sketch, "E355.right", {"start": v(710, 25.08) * mm, "end": v(710, 19.07) * mm});
            skLineSegment(sketch, "E356.trimOffspring", {"start": v(-25, -338.02) * mm, "end": v(-25, -499.92) * mm});
            skLineSegment(sketch, "E357.trimOffspring", {"start": v(170, 25.08) * mm, "end": v(331.9, 25.08) * mm});
            skLineSegment(sketch, "E358.trimOffspring", {"start": v(350, 25.08) * mm, "end": v(511.9, 25.08) * mm});
            skLineSegment(sketch, "E359.trimOffspring", {"start": v(530, 25.08) * mm, "end": v(691.9, 25.08) * mm});
            skLineSegment(sketch, "E360.trimOffspring", {"start": v(710, 25.08) * mm, "end": v(875, 25.08) * mm});
            skLineSegment(sketch, "E361.bottom", {"start": v(165, -193.9) * mm, "end": v(171.01, -193.9) * mm});
            skLineSegment(sketch, "E361.top", {"start": v(165, -212) * mm, "end": v(171.01, -212) * mm});
            skLineSegment(sketch, "E361.left", {"start": v(165, -193.9) * mm, "end": v(165, -212) * mm});
            skLineSegment(sketch, "E361.right", {"start": v(171.01, -193.9) * mm, "end": v(171.01, -212) * mm});
            skPoint(sketch, "E362.firstSnap0", {"position": v(168, -193.9) * mm});
            skPoint(sketch, "E362.oppositeSnap0", {"position": v(168, -212) * mm});
            skLineSegment(sketch, "E362.bottom", {"start": v(330.2, -193.9) * mm, "end": v(336.21, -193.9) * mm});
            skLineSegment(sketch, "E362.top", {"start": v(330.2, -212) * mm, "end": v(336.21, -212) * mm});
            skLineSegment(sketch, "E362.left", {"start": v(330.2, -193.9) * mm, "end": v(330.2, -212) * mm});
            skLineSegment(sketch, "E362.right", {"start": v(336.21, -193.9) * mm, "end": v(336.21, -212) * mm});
            skLineSegment(sketch, "E363.bottom", {"start": v(513.8, -193.9) * mm, "end": v(519.8, -193.9) * mm});
            skLineSegment(sketch, "E363.top", {"start": v(513.8, -212) * mm, "end": v(519.8, -212) * mm});
            skLineSegment(sketch, "E363.left", {"start": v(513.8, -193.9) * mm, "end": v(513.8, -212) * mm});
            skLineSegment(sketch, "E363.right", {"start": v(519.8, -193.9) * mm, "end": v(519.8, -212) * mm});
            skLineSegment(sketch, "E364.bottom", {"start": v(679, -193.9) * mm, "end": v(685, -193.9) * mm});
            skLineSegment(sketch, "E364.top", {"start": v(679, -212) * mm, "end": v(685, -212) * mm});
            skLineSegment(sketch, "E364.left", {"start": v(679, -193.9) * mm, "end": v(679, -212) * mm});
            skLineSegment(sketch, "E364.right", {"start": v(685, -193.9) * mm, "end": v(685, -212) * mm});
            skLineSegment(sketch, "E365.bottom", {"start": v(165, -415.91) * mm, "end": v(171.01, -415.91) * mm});
            skLineSegment(sketch, "E365.top", {"start": v(165, -434) * mm, "end": v(171.01, -434) * mm});
            skLineSegment(sketch, "E365.left", {"start": v(165, -415.91) * mm, "end": v(165, -434) * mm});
            skLineSegment(sketch, "E365.right", {"start": v(171.01, -415.91) * mm, "end": v(171.01, -434) * mm});
            skLineSegment(sketch, "E366.bottom", {"start": v(165, -637.9) * mm, "end": v(171.01, -637.9) * mm});
            skLineSegment(sketch, "E366.top", {"start": v(165, -656) * mm, "end": v(171.01, -656) * mm});
            skLineSegment(sketch, "E366.left", {"start": v(165, -637.9) * mm, "end": v(165, -656) * mm});
            skLineSegment(sketch, "E366.right", {"start": v(171.01, -637.9) * mm, "end": v(171.01, -656) * mm});
            skLineSegment(sketch, "E367.bottom", {"start": v(330.2, -415.91) * mm, "end": v(336.21, -415.91) * mm});
            skLineSegment(sketch, "E367.top", {"start": v(330.2, -434) * mm, "end": v(336.21, -434) * mm});
            skLineSegment(sketch, "E367.left", {"start": v(330.2, -415.91) * mm, "end": v(330.2, -434) * mm});
            skLineSegment(sketch, "E367.right", {"start": v(336.21, -415.91) * mm, "end": v(336.21, -434) * mm});
            skLineSegment(sketch, "E368.bottom", {"start": v(513.8, -415.91) * mm, "end": v(519.8, -415.91) * mm});
            skLineSegment(sketch, "E368.top", {"start": v(513.8, -434) * mm, "end": v(519.8, -434) * mm});
            skLineSegment(sketch, "E368.left", {"start": v(513.8, -415.91) * mm, "end": v(513.8, -434) * mm});
            skLineSegment(sketch, "E368.right", {"start": v(519.8, -415.91) * mm, "end": v(519.8, -434) * mm});
            skLineSegment(sketch, "E369.bottom", {"start": v(679, -415.91) * mm, "end": v(685, -415.91) * mm});
            skLineSegment(sketch, "E369.top", {"start": v(679, -434) * mm, "end": v(685, -434) * mm});
            skLineSegment(sketch, "E369.left", {"start": v(679, -415.91) * mm, "end": v(679, -434) * mm});
            skLineSegment(sketch, "E369.right", {"start": v(685, -415.91) * mm, "end": v(685, -434) * mm});
            skPoint(sketch, "E370.firstSnap0", {"position": v(330.2, -424.96) * mm});
            skLineSegment(sketch, "E370.bottom", {"start": v(330.2, -637.9) * mm, "end": v(336.21, -637.9) * mm});
            skLineSegment(sketch, "E370.top", {"start": v(330.2, -656) * mm, "end": v(336.21, -656) * mm});
            skLineSegment(sketch, "E370.left", {"start": v(330.2, -637.9) * mm, "end": v(330.2, -656) * mm});
            skLineSegment(sketch, "E370.right", {"start": v(336.21, -637.9) * mm, "end": v(336.21, -656) * mm});
            skLineSegment(sketch, "E371.bottom", {"start": v(513.8, -637.9) * mm, "end": v(519.8, -637.9) * mm});
            skLineSegment(sketch, "E371.top", {"start": v(513.8, -656) * mm, "end": v(519.8, -656) * mm});
            skLineSegment(sketch, "E371.left", {"start": v(513.8, -637.9) * mm, "end": v(513.8, -656) * mm});
            skLineSegment(sketch, "E371.right", {"start": v(519.8, -637.9) * mm, "end": v(519.8, -656) * mm});
            skLineSegment(sketch, "E372.bottom", {"start": v(679, -637.9) * mm, "end": v(685, -637.9) * mm});
            skLineSegment(sketch, "E372.top", {"start": v(679, -656) * mm, "end": v(685, -656) * mm});
            skLineSegment(sketch, "E372.left", {"start": v(679, -637.9) * mm, "end": v(679, -656) * mm});
            skLineSegment(sketch, "E372.right", {"start": v(685, -637.9) * mm, "end": v(685, -656) * mm});
            skLineSegment(sketch, "E373.bottom", {"start": v(194, -684.92) * mm, "end": v(212.01, -684.92) * mm});
            skLineSegment(sketch, "E373.top", {"start": v(194, -678.91) * mm, "end": v(212.01, -678.91) * mm});
            skLineSegment(sketch, "E373.left", {"start": v(194, -684.92) * mm, "end": v(194, -678.91) * mm});
            skLineSegment(sketch, "E373.right", {"start": v(212.01, -684.92) * mm, "end": v(212.01, -678.91) * mm});
            skLineSegment(sketch, "E374.bottom", {"start": v(434.01, -684.92) * mm, "end": v(416, -684.92) * mm});
            skLineSegment(sketch, "E374.top", {"start": v(434.01, -678.91) * mm, "end": v(416, -678.91) * mm});
            skLineSegment(sketch, "E374.left", {"start": v(434.01, -684.92) * mm, "end": v(434.01, -678.91) * mm});
            skLineSegment(sketch, "E374.right", {"start": v(416, -684.92) * mm, "end": v(416, -678.91) * mm});
            skLineSegment(sketch, "E375.bottom", {"start": v(656.01, -684.92) * mm, "end": v(638, -684.92) * mm});
            skLineSegment(sketch, "E375.top", {"start": v(656.01, -678.91) * mm, "end": v(638, -678.91) * mm});
            skLineSegment(sketch, "E375.left", {"start": v(656.01, -684.92) * mm, "end": v(656.01, -678.91) * mm});
            skLineSegment(sketch, "E375.right", {"start": v(638, -684.92) * mm, "end": v(638, -678.91) * mm});
            skLineSegment(sketch, "E376.bottom", {"start": v(212.01, -519.72) * mm, "end": v(194, -519.72) * mm});
            skLineSegment(sketch, "E376.top", {"start": v(212.01, -513.71) * mm, "end": v(194, -513.71) * mm});
            skLineSegment(sketch, "E376.left", {"start": v(212.01, -519.72) * mm, "end": v(212.01, -513.71) * mm});
            skLineSegment(sketch, "E376.right", {"start": v(194, -519.72) * mm, "end": v(194, -513.71) * mm});
            skLineSegment(sketch, "E377.bottom", {"start": v(212.01, -336.13) * mm, "end": v(194, -336.13) * mm});
            skLineSegment(sketch, "E377.top", {"start": v(212.01, -330.12) * mm, "end": v(194, -330.12) * mm});
            skLineSegment(sketch, "E377.left", {"start": v(212.01, -336.13) * mm, "end": v(212.01, -330.12) * mm});
            skLineSegment(sketch, "E377.right", {"start": v(194, -336.13) * mm, "end": v(194, -330.12) * mm});
            skLineSegment(sketch, "E378.bottom", {"start": v(212.01, -170.93) * mm, "end": v(194, -170.93) * mm});
            skLineSegment(sketch, "E378.top", {"start": v(212.01, -164.92) * mm, "end": v(194, -164.92) * mm});
            skLineSegment(sketch, "E378.left", {"start": v(212.01, -170.93) * mm, "end": v(212.01, -164.92) * mm});
            skLineSegment(sketch, "E378.right", {"start": v(194, -170.93) * mm, "end": v(194, -164.92) * mm});
            skLineSegment(sketch, "E379.bottom", {"start": v(434.01, -513.71) * mm, "end": v(416, -513.71) * mm});
            skLineSegment(sketch, "E379.top", {"start": v(434, -519.72) * mm, "end": v(416, -519.72) * mm});
            skLineSegment(sketch, "E379.left", {"start": v(434.01, -513.71) * mm, "end": v(434.01, -519.72) * mm});
            skLineSegment(sketch, "E379.right", {"start": v(416, -513.71) * mm, "end": v(416, -519.72) * mm});
            skLineSegment(sketch, "E380.bottom", {"start": v(656.01, -519.72) * mm, "end": v(637.99, -519.72) * mm});
            skLineSegment(sketch, "E380.top", {"start": v(656.01, -513.71) * mm, "end": v(637.99, -513.71) * mm});
            skLineSegment(sketch, "E380.left", {"start": v(656.01, -519.72) * mm, "end": v(656.01, -513.71) * mm});
            skLineSegment(sketch, "E380.right", {"start": v(638, -519.72) * mm, "end": v(638, -513.71) * mm});
            skLineSegment(sketch, "E381.bottom", {"start": v(434, -336.13) * mm, "end": v(415.99, -336.13) * mm});
            skLineSegment(sketch, "E381.top", {"start": v(434, -330.12) * mm, "end": v(415.99, -330.12) * mm});
            skLineSegment(sketch, "E381.left", {"start": v(434.01, -336.13) * mm, "end": v(434.01, -330.12) * mm});
            skLineSegment(sketch, "E381.right", {"start": v(416, -336.13) * mm, "end": v(416, -330.12) * mm});
            skLineSegment(sketch, "E382.bottom", {"start": v(656.01, -330.12) * mm, "end": v(637.99, -330.12) * mm});
            skLineSegment(sketch, "E382.top", {"start": v(656.01, -336.13) * mm, "end": v(637.99, -336.13) * mm});
            skLineSegment(sketch, "E382.left", {"start": v(656.01, -330.12) * mm, "end": v(656.01, -336.13) * mm});
            skLineSegment(sketch, "E382.right", {"start": v(638, -330.12) * mm, "end": v(638, -336.13) * mm});
            skLineSegment(sketch, "E383.bottom", {"start": v(434, -164.92) * mm, "end": v(415.99, -164.92) * mm});
            skLineSegment(sketch, "E383.top", {"start": v(434, -170.93) * mm, "end": v(415.99, -170.93) * mm});
            skLineSegment(sketch, "E383.left", {"start": v(434.01, -164.92) * mm, "end": v(434.01, -170.93) * mm});
            skLineSegment(sketch, "E383.right", {"start": v(416, -164.92) * mm, "end": v(416, -170.93) * mm});
            skLineSegment(sketch, "E384.bottom", {"start": v(656.01, -164.92) * mm, "end": v(637.99, -164.92) * mm});
            skLineSegment(sketch, "E384.top", {"start": v(656.01, -170.93) * mm, "end": v(637.99, -170.93) * mm});
            skLineSegment(sketch, "E384.left", {"start": v(656.01, -164.92) * mm, "end": v(656.01, -170.93) * mm});
            skLineSegment(sketch, "E384.right", {"start": v(638, -164.92) * mm, "end": v(638, -170.93) * mm});
            skSolve(sketch);
        }
        {
            var Q0;
            Q0 = qSketchRegion(id + "F0", true);
            extrude(context, id + "F1", {"entities" : qUnion([Q0]), "depth" : 6 * mm, "offsetDistance" : 25 * mm});
        }
        {
            var Q0;
            Q0=qCreatedBy(makeId("Front.planeOp"),FACE);
            var sketch = newSketch(context, id + "F2", { "sketchPlane" : qUnion([Q0])});
            skLineSegment(sketch, "E385.bottom", {"start": v(-30.63, -176.03) * mm, "end": v(140.37, -176.03) * mm});
            skLineSegment(sketch, "E385.top", {"start": v(-30.63, -320.03) * mm, "end": v(869.37, -320.03) * mm});
            skPoint(sketch, "E386.orphan", {"position": v(-25.02, 5.3) * mm});
            skLineSegment(sketch, "E387", {"start": v(-30.63, -320.03) * mm, "end": v(-30.63, -297.27) * mm});
            skLineSegment(sketch, "E388", {"start": v(869.37, -176.03) * mm, "end": v(869.37, -211.24) * mm});
            skLineSegment(sketch, "E389", {"start": v(140.37, -176.03) * mm, "end": v(140.37, -170.23) * mm});
            skLineSegment(sketch, "E390", {"start": v(140.37, -170.23) * mm, "end": v(142.37, -170.23) * mm});
            skLineSegment(sketch, "E391", {"start": v(142.37, -170.23) * mm, "end": v(144.37, -173.03) * mm});
            skLineSegment(sketch, "E392", {"start": v(144.37, -173.03) * mm, "end": v(154.37, -173.03) * mm});
            skLineSegment(sketch, "E393", {"start": v(154.37, -173.03) * mm, "end": v(156.37, -170.23) * mm});
            skLineSegment(sketch, "E394", {"start": v(156.37, -170.23) * mm, "end": v(158.37, -170.23) * mm});
            skLineSegment(sketch, "E395", {"start": v(158.37, -170.23) * mm, "end": v(158.37, -176.03) * mm});
            skLineSegment(sketch, "E396.trimOffspring", {"start": v(158.37, -176.03) * mm, "end": v(320.37, -176.03) * mm});
            skLineSegment(sketch, "E397.trimOffspring", {"start": v(338.37, -176.03) * mm, "end": v(500.37, -176.03) * mm});
            skLineSegment(sketch, "E398", {"start": v(500.37, -176.03) * mm, "end": v(500.37, -170.23) * mm});
            skLineSegment(sketch, "E399", {"start": v(500.37, -170.23) * mm, "end": v(502.37, -170.23) * mm});
            skLineSegment(sketch, "E400", {"start": v(502.37, -170.23) * mm, "end": v(504.37, -173.03) * mm});
            skLineSegment(sketch, "E401", {"start": v(504.37, -173.03) * mm, "end": v(514.37, -173.03) * mm});
            skLineSegment(sketch, "E402", {"start": v(514.37, -173.03) * mm, "end": v(516.37, -170.23) * mm});
            skLineSegment(sketch, "E403", {"start": v(516.37, -170.23) * mm, "end": v(518.37, -170.23) * mm});
            skLineSegment(sketch, "E404", {"start": v(518.37, -170.23) * mm, "end": v(518.37, -176.03) * mm});
            skLineSegment(sketch, "E405.trimOffspring", {"start": v(518.37, -176.03) * mm, "end": v(680.37, -176.03) * mm});
            skLineSegment(sketch, "E406", {"start": v(680.37, -176.03) * mm, "end": v(680.37, -170.23) * mm});
            skLineSegment(sketch, "E407", {"start": v(680.37, -170.23) * mm, "end": v(682.37, -170.23) * mm});
            skLineSegment(sketch, "E408", {"start": v(682.37, -170.23) * mm, "end": v(684.37, -173.03) * mm});
            skLineSegment(sketch, "E409", {"start": v(684.37, -173.03) * mm, "end": v(694.37, -173.03) * mm});
            skLineSegment(sketch, "E410", {"start": v(694.37, -173.03) * mm, "end": v(696.37, -170.23) * mm});
            skLineSegment(sketch, "E411", {"start": v(696.37, -170.23) * mm, "end": v(698.37, -170.23) * mm});
            skLineSegment(sketch, "E412", {"start": v(698.37, -170.23) * mm, "end": v(698.37, -176.03) * mm});
            skLineSegment(sketch, "E413.trimOffspring", {"start": v(698.37, -176.03) * mm, "end": v(869.37, -176.03) * mm});
            skLineSegment(sketch, "E414", {"start": v(-30.63, -195.03) * mm, "end": v(869.37, -195.03) * mm, "construction": true});
            skCircle(sketch, "E415", {"center": v(-5.63, -195.03) * mm, "radius": 8 * mm});
            skCircle(sketch, "E416", {"center": v(44.37, -195.03) * mm, "radius": 8 * mm});
            skCircle(sketch, "E417", {"center": v(94.37, -195.03) * mm, "radius": 8 * mm});
            skCircle(sketch, "E418", {"center": v(144.37, -195.03) * mm, "radius": 8 * mm});
            skCircle(sketch, "E419", {"center": v(194.37, -195.03) * mm, "radius": 8 * mm});
            skCircle(sketch, "E420", {"center": v(244.37, -195.03) * mm, "radius": 8 * mm});
            skCircle(sketch, "E421", {"center": v(294.37, -195.03) * mm, "radius": 8 * mm});
            skCircle(sketch, "E422", {"center": v(344.37, -195.03) * mm, "radius": 8 * mm});
            skCircle(sketch, "E423", {"center": v(394.37, -195.03) * mm, "radius": 8 * mm});
            skCircle(sketch, "E424", {"center": v(444.37, -195.03) * mm, "radius": 8 * mm});
            skCircle(sketch, "E425", {"center": v(494.37, -195.03) * mm, "radius": 8 * mm});
            skCircle(sketch, "E426", {"center": v(544.37, -195.03) * mm, "radius": 8 * mm});
            skCircle(sketch, "E427", {"center": v(594.37, -195.03) * mm, "radius": 8 * mm});
            skCircle(sketch, "E428", {"center": v(644.37, -195.03) * mm, "radius": 8 * mm});
            skCircle(sketch, "E429", {"center": v(744.37, -195.03) * mm, "radius": 8 * mm});
            skCircle(sketch, "E430", {"center": v(694.37, -195.03) * mm, "radius": 8 * mm});
            skCircle(sketch, "E431", {"center": v(794.37, -195.03) * mm, "radius": 8 * mm});
            skCircle(sketch, "E432", {"center": v(844.37, -195.03) * mm, "radius": 8 * mm});
            skLineSegment(sketch, "E433", {"start": v(-5.63, -195.03) * mm, "end": v(-5.63, -355.88) * mm, "construction": true});
            skLineSegment(sketch, "E434", {"start": v(-30.63, -245.03) * mm, "end": v(869.37, -245.03) * mm, "construction": true});
            skCircle(sketch, "E435", {"center": v(-5.63, -245.03) * mm, "radius": 8 * mm});
            skCircle(sketch, "E436", {"center": v(44.37, -245.03) * mm, "radius": 8 * mm});
            skCircle(sketch, "E437", {"center": v(94.37, -245.03) * mm, "radius": 8 * mm});
            skCircle(sketch, "E438", {"center": v(144.37, -245.03) * mm, "radius": 8 * mm});
            skCircle(sketch, "E439", {"center": v(194.37, -245.03) * mm, "radius": 8 * mm});
            skCircle(sketch, "E440", {"center": v(244.37, -245.03) * mm, "radius": 8 * mm});
            skCircle(sketch, "E441", {"center": v(294.37, -245.03) * mm, "radius": 8 * mm});
            skCircle(sketch, "E442", {"center": v(344.37, -245.03) * mm, "radius": 8 * mm});
            skCircle(sketch, "E443", {"center": v(394.37, -245.03) * mm, "radius": 8 * mm});
            skCircle(sketch, "E444", {"center": v(444.37, -245.03) * mm, "radius": 8 * mm});
            skCircle(sketch, "E445", {"center": v(494.37, -245.03) * mm, "radius": 8 * mm});
            skCircle(sketch, "E446", {"center": v(544.37, -245.03) * mm, "radius": 8 * mm});
            skCircle(sketch, "E447", {"center": v(594.37, -245.03) * mm, "radius": 8 * mm});
            skCircle(sketch, "E448", {"center": v(644.37, -245.03) * mm, "radius": 8 * mm});
            skCircle(sketch, "E449", {"center": v(744.37, -245.03) * mm, "radius": 8 * mm});
            skCircle(sketch, "E450", {"center": v(694.37, -245.03) * mm, "radius": 8 * mm});
            skCircle(sketch, "E451", {"center": v(794.37, -245.03) * mm, "radius": 8 * mm});
            skCircle(sketch, "E452", {"center": v(844.37, -245.03) * mm, "radius": 8 * mm});
            skLineSegment(sketch, "E453", {"start": v(-30.63, -295.03) * mm, "end": v(869.37, -295.03) * mm, "construction": true});
            skCircle(sketch, "E454", {"center": v(-5.63, -295.03) * mm, "radius": 8 * mm});
            skCircle(sketch, "E455", {"center": v(44.37, -295.03) * mm, "radius": 8 * mm});
            skCircle(sketch, "E456", {"center": v(94.37, -295.03) * mm, "radius": 8 * mm});
            skCircle(sketch, "E457", {"center": v(144.37, -295.03) * mm, "radius": 8 * mm});
            skCircle(sketch, "E458", {"center": v(194.37, -295.03) * mm, "radius": 8 * mm});
            skCircle(sketch, "E459", {"center": v(244.37, -295.03) * mm, "radius": 8 * mm});
            skCircle(sketch, "E460", {"center": v(294.37, -295.03) * mm, "radius": 8 * mm});
            skCircle(sketch, "E461", {"center": v(344.37, -295.03) * mm, "radius": 8 * mm});
            skCircle(sketch, "E462", {"center": v(394.37, -295.03) * mm, "radius": 8 * mm});
            skCircle(sketch, "E463", {"center": v(444.37, -295.03) * mm, "radius": 8 * mm});
            skCircle(sketch, "E464", {"center": v(494.37, -295.03) * mm, "radius": 8 * mm});
            skCircle(sketch, "E465", {"center": v(544.37, -295.03) * mm, "radius": 8 * mm});
            skCircle(sketch, "E466", {"center": v(594.37, -295.03) * mm, "radius": 8 * mm});
            skCircle(sketch, "E467", {"center": v(644.37, -295.03) * mm, "radius": 8 * mm});
            skCircle(sketch, "E468", {"center": v(744.37, -295.03) * mm, "radius": 8 * mm});
            skCircle(sketch, "E469", {"center": v(694.37, -295.03) * mm, "radius": 8 * mm});
            skCircle(sketch, "E470", {"center": v(794.37, -295.03) * mm, "radius": 8 * mm});
            skCircle(sketch, "E471", {"center": v(844.37, -295.03) * mm, "radius": 8 * mm});
            skLineSegment(sketch, "E472", {"start": v(-30.63, -211.23) * mm, "end": v(-24.62, -211.23) * mm});
            skLineSegment(sketch, "E473", {"start": v(-24.62, -211.23) * mm, "end": v(-24.62, -229.25) * mm});
            skLineSegment(sketch, "E474", {"start": v(-24.62, -229.25) * mm, "end": v(-30.63, -229.25) * mm});
            skLineSegment(sketch, "E475", {"start": v(-30.63, -279.25) * mm, "end": v(-24.62, -279.25) * mm});
            skLineSegment(sketch, "E476", {"start": v(-24.62, -279.25) * mm, "end": v(-24.62, -297.27) * mm});
            skLineSegment(sketch, "E477", {"start": v(-24.62, -297.27) * mm, "end": v(-30.63, -297.27) * mm});
            skLineSegment(sketch, "E478.trimOffspring", {"start": v(-30.63, -211.23) * mm, "end": v(-30.63, -176.03) * mm});
            skLineSegment(sketch, "E479.trimOffspring", {"start": v(-30.63, -279.25) * mm, "end": v(-30.63, -229.25) * mm});
            skLineSegment(sketch, "E480", {"start": v(869.37, -211.24) * mm, "end": v(875.17, -211.24) * mm});
            skLineSegment(sketch, "E481", {"start": v(875.17, -211.24) * mm, "end": v(875.17, -213.24) * mm});
            skLineSegment(sketch, "E482", {"start": v(875.17, -213.24) * mm, "end": v(872.37, -215.24) * mm});
            skLineSegment(sketch, "E483", {"start": v(872.37, -215.24) * mm, "end": v(872.37, -225.24) * mm});
            skLineSegment(sketch, "E484", {"start": v(872.37, -225.24) * mm, "end": v(875.17, -227.24) * mm});
            skLineSegment(sketch, "E485", {"start": v(875.17, -227.24) * mm, "end": v(875.17, -229.24) * mm});
            skLineSegment(sketch, "E486", {"start": v(875.17, -229.24) * mm, "end": v(869.37, -229.24) * mm});
            skLineSegment(sketch, "E487", {"start": v(869.37, -279.26) * mm, "end": v(875.17, -279.26) * mm});
            skLineSegment(sketch, "E488", {"start": v(875.17, -279.26) * mm, "end": v(875.17, -281.26) * mm});
            skLineSegment(sketch, "E489", {"start": v(875.17, -281.26) * mm, "end": v(872.37, -283.26) * mm});
            skLineSegment(sketch, "E490", {"start": v(872.37, -283.26) * mm, "end": v(872.37, -293.26) * mm});
            skLineSegment(sketch, "E491", {"start": v(872.37, -293.26) * mm, "end": v(875.17, -295.26) * mm});
            skLineSegment(sketch, "E492", {"start": v(875.17, -295.26) * mm, "end": v(875.17, -297.26) * mm});
            skLineSegment(sketch, "E493", {"start": v(875.17, -297.26) * mm, "end": v(869.37, -297.26) * mm});
            skLineSegment(sketch, "E494.trimOffspring", {"start": v(869.37, -229.24) * mm, "end": v(869.37, -279.26) * mm});
            skLineSegment(sketch, "E495.trimOffspring", {"start": v(869.37, -297.26) * mm, "end": v(869.37, -320.03) * mm});
            skLineSegment(sketch, "E496", {"start": v(320.37, -176.03) * mm, "end": v(320.37, -170.23) * mm});
            skLineSegment(sketch, "E497", {"start": v(320.37, -170.23) * mm, "end": v(322.37, -170.23) * mm});
            skLineSegment(sketch, "E498", {"start": v(322.37, -170.23) * mm, "end": v(324.37, -173.03) * mm});
            skLineSegment(sketch, "E499", {"start": v(324.37, -173.03) * mm, "end": v(334.37, -173.03) * mm});
            skLineSegment(sketch, "E500", {"start": v(334.37, -173.03) * mm, "end": v(336.37, -170.23) * mm});
            skLineSegment(sketch, "E501", {"start": v(336.37, -170.23) * mm, "end": v(338.37, -170.23) * mm});
            skLineSegment(sketch, "E502", {"start": v(338.37, -170.23) * mm, "end": v(338.37, -176.03) * mm});
            skSolve(sketch);
        }
        {
            var Q0;
            Q0=makeQuery(id+"F2.imprint","IMPRINT",FACE,{"disambiguationData":[TD([[makeQuery(id+"F2.imprint","IMPRINT",EDGE,{"derivedFrom":sQuery(id+"F2.wireOp",EDGE,"E385.bottom")}),-1.0]])]});
            extrude(context, id + "F3", {"entities" : qUnion([Q0]), "depth" : 6 * mm, "offsetDistance" : 25 * mm});
        }
        {
            var Q0;
            Q0=makeQuery(id+"F3.opExtrude","SWEPT_BODY",BODY,{"disambiguationData":[OSD([sQuery(id+"F2.wireOp",EDGE,"E385.bottom"),sQuery(id+"F2.wireOp",EDGE,"E385.top"),sQuery(id+"F2.wireOp",EDGE,"E387"),sQuery(id+"F2.wireOp",EDGE,"E388"),sQuery(id+"F2.wireOp",EDGE,"E389"),sQuery(id+"F2.wireOp",EDGE,"E390"),sQuery(id+"F2.wireOp",EDGE,"E391"),sQuery(id+"F2.wireOp",EDGE,"E392"),sQuery(id+"F2.wireOp",EDGE,"E393"),sQuery(id+"F2.wireOp",EDGE,"E394"),sQuery(id+"F2.wireOp",EDGE,"E395"),sQuery(id+"F2.wireOp",EDGE,"E396.trimOffspring"),sQuery(id+"F2.wireOp",EDGE,"E397.trimOffspring"),sQuery(id+"F2.wireOp",EDGE,"E398"),sQuery(id+"F2.wireOp",EDGE,"E399"),sQuery(id+"F2.wireOp",EDGE,"E400"),sQuery(id+"F2.wireOp",EDGE,"E401"),sQuery(id+"F2.wireOp",EDGE,"E402"),sQuery(id+"F2.wireOp",EDGE,"E403"),sQuery(id+"F2.wireOp",EDGE,"E404"),sQuery(id+"F2.wireOp",EDGE,"E405.trimOffspring"),sQuery(id+"F2.wireOp",EDGE,"E406"),sQuery(id+"F2.wireOp",EDGE,"E407"),sQuery(id+"F2.wireOp",EDGE,"E408"),sQuery(id+"F2.wireOp",EDGE,"E409"),sQuery(id+"F2.wireOp",EDGE,"E410"),sQuery(id+"F2.wireOp",EDGE,"E411"),sQuery(id+"F2.wireOp",EDGE,"E412"),sQuery(id+"F2.wireOp",EDGE,"E413.trimOffspring"),sQuery(id+"F2.wireOp",EDGE,"E415"),sQuery(id+"F2.wireOp",EDGE,"E416"),sQuery(id+"F2.wireOp",EDGE,"E417"),sQuery(id+"F2.wireOp",EDGE,"E418"),sQuery(id+"F2.wireOp",EDGE,"E419"),sQuery(id+"F2.wireOp",EDGE,"E420"),sQuery(id+"F2.wireOp",EDGE,"E421"),sQuery(id+"F2.wireOp",EDGE,"E422"),sQuery(id+"F2.wireOp",EDGE,"E423"),sQuery(id+"F2.wireOp",EDGE,"E424"),sQuery(id+"F2.wireOp",EDGE,"E425"),sQuery(id+"F2.wireOp",EDGE,"E426"),sQuery(id+"F2.wireOp",EDGE,"E427"),sQuery(id+"F2.wireOp",EDGE,"E428"),sQuery(id+"F2.wireOp",EDGE,"E429"),sQuery(id+"F2.wireOp",EDGE,"E430"),sQuery(id+"F2.wireOp",EDGE,"E431"),sQuery(id+"F2.wireOp",EDGE,"E432"),sQuery(id+"F2.wireOp",EDGE,"E435"),sQuery(id+"F2.wireOp",EDGE,"E436"),sQuery(id+"F2.wireOp",EDGE,"E437"),sQuery(id+"F2.wireOp",EDGE,"E438"),sQuery(id+"F2.wireOp",EDGE,"E439"),sQuery(id+"F2.wireOp",EDGE,"E440"),sQuery(id+"F2.wireOp",EDGE,"E441"),sQuery(id+"F2.wireOp",EDGE,"E442"),sQuery(id+"F2.wireOp",EDGE,"E443"),sQuery(id+"F2.wireOp",EDGE,"E444"),sQuery(id+"F2.wireOp",EDGE,"E445"),sQuery(id+"F2.wireOp",EDGE,"E446"),sQuery(id+"F2.wireOp",EDGE,"E447"),sQuery(id+"F2.wireOp",EDGE,"E448"),sQuery(id+"F2.wireOp",EDGE,"E449"),sQuery(id+"F2.wireOp",EDGE,"E450"),sQuery(id+"F2.wireOp",EDGE,"E451"),sQuery(id+"F2.wireOp",EDGE,"E452"),sQuery(id+"F2.wireOp",EDGE,"E454"),sQuery(id+"F2.wireOp",EDGE,"E455"),sQuery(id+"F2.wireOp",EDGE,"E456"),sQuery(id+"F2.wireOp",EDGE,"E457"),sQuery(id+"F2.wireOp",EDGE,"E458"),sQuery(id+"F2.wireOp",EDGE,"E459"),sQuery(id+"F2.wireOp",EDGE,"E460"),sQuery(id+"F2.wireOp",EDGE,"E461"),sQuery(id+"F2.wireOp",EDGE,"E462"),sQuery(id+"F2.wireOp",EDGE,"E463"),sQuery(id+"F2.wireOp",EDGE,"E464"),sQuery(id+"F2.wireOp",EDGE,"E465"),sQuery(id+"F2.wireOp",EDGE,"E466"),sQuery(id+"F2.wireOp",EDGE,"E467"),sQuery(id+"F2.wireOp",EDGE,"E468"),sQuery(id+"F2.wireOp",EDGE,"E469"),sQuery(id+"F2.wireOp",EDGE,"E470"),sQuery(id+"F2.wireOp",EDGE,"E471"),sQuery(id+"F2.wireOp",EDGE,"E472"),sQuery(id+"F2.wireOp",EDGE,"E473"),sQuery(id+"F2.wireOp",EDGE,"E474"),sQuery(id+"F2.wireOp",EDGE,"E475"),sQuery(id+"F2.wireOp",EDGE,"E476"),sQuery(id+"F2.wireOp",EDGE,"E477"),sQuery(id+"F2.wireOp",EDGE,"E478.trimOffspring"),sQuery(id+"F2.wireOp",EDGE,"E479.trimOffspring"),sQuery(id+"F2.wireOp",EDGE,"E480"),sQuery(id+"F2.wireOp",EDGE,"E481"),sQuery(id+"F2.wireOp",EDGE,"E482"),sQuery(id+"F2.wireOp",EDGE,"E483"),sQuery(id+"F2.wireOp",EDGE,"E484"),sQuery(id+"F2.wireOp",EDGE,"E485"),sQuery(id+"F2.wireOp",EDGE,"E486"),sQuery(id+"F2.wireOp",EDGE,"E487"),sQuery(id+"F2.wireOp",EDGE,"E488"),sQuery(id+"F2.wireOp",EDGE,"E489"),sQuery(id+"F2.wireOp",EDGE,"E490"),sQuery(id+"F2.wireOp",EDGE,"E491"),sQuery(id+"F2.wireOp",EDGE,"E492"),sQuery(id+"F2.wireOp",EDGE,"E493"),sQuery(id+"F2.wireOp",EDGE,"E494.trimOffspring"),sQuery(id+"F2.wireOp",EDGE,"E495.trimOffspring"),sQuery(id+"F2.wireOp",EDGE,"E496"),sQuery(id+"F2.wireOp",EDGE,"E497"),sQuery(id+"F2.wireOp",EDGE,"E498"),sQuery(id+"F2.wireOp",EDGE,"E499"),sQuery(id+"F2.wireOp",EDGE,"E500"),sQuery(id+"F2.wireOp",EDGE,"E501"),sQuery(id+"F2.wireOp",EDGE,"E502")])]});
            deleteBodies(context, id + "F4", {"entities" : qUnion([Q0])});
        }
    });
